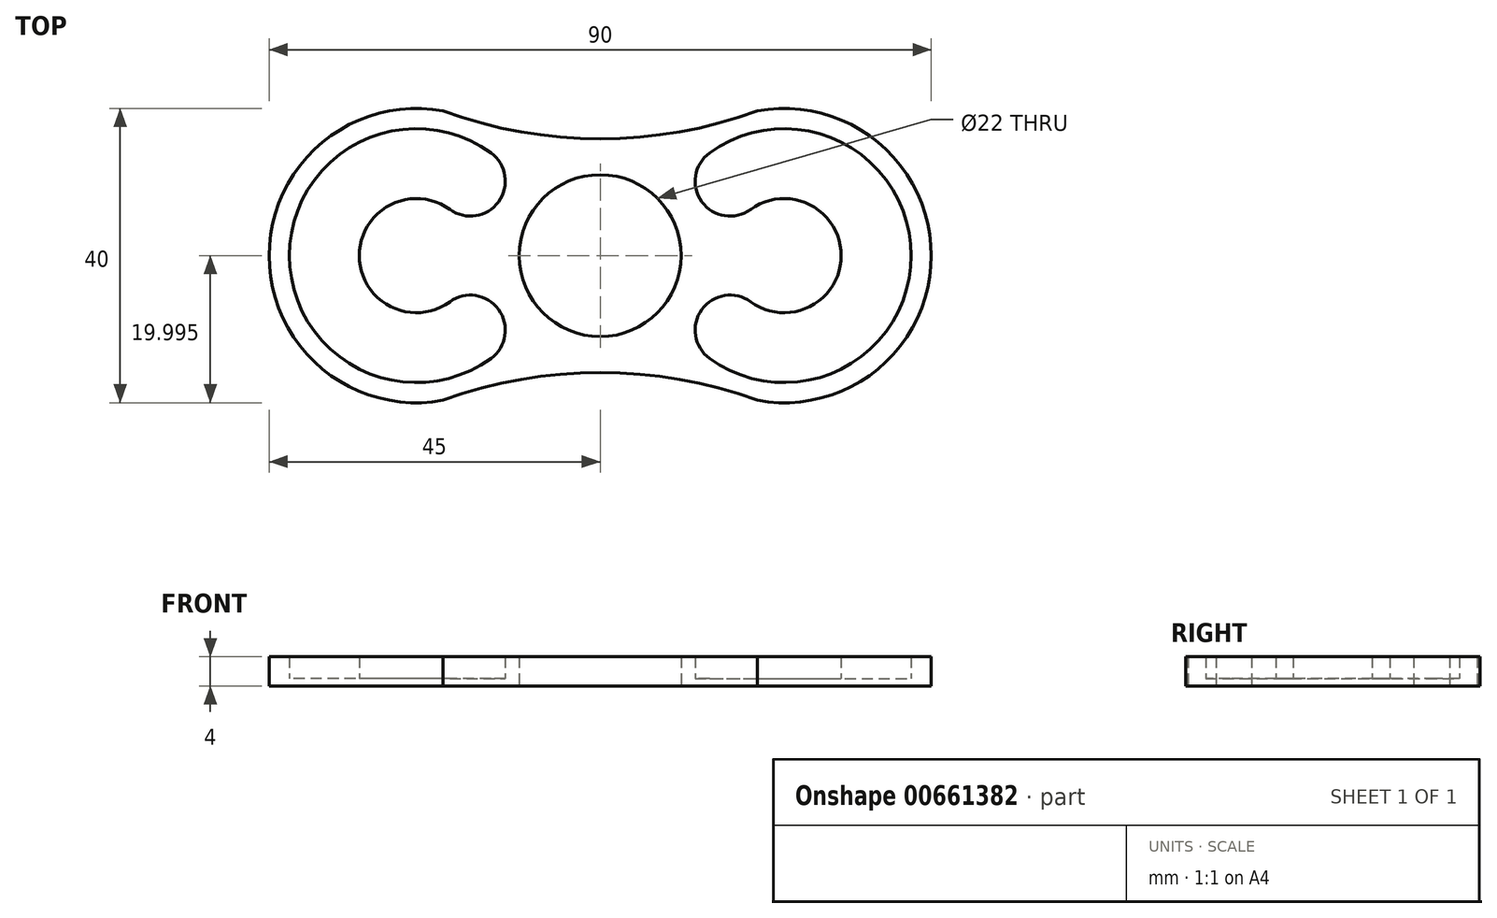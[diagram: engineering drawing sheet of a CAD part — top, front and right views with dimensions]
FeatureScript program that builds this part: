
annotation { "Feature Type Name" : "Feature", "Feature Type Description" : "" }
export const myFeature = defineFeature(function(context is Context, id is Id, definition is map)
    precondition{}
    {
        {
            var Q0;
            Q0=qCreatedBy(makeId("Top.planeOp"),FACE);
            var sketch = newSketch(context, id + "F0", { "sketchPlane" : qUnion([Q0])});
            skCircle(sketch, "E0", {"center": v(25, 38.36) * mm, "radius": 11 * mm});
            skCircle(sketch, "E1", {"center": v(25, 38.36) * mm, "radius": 15 * mm});
            skCircle(sketch, "E2", {"center": v(0, 38.36) * mm, "radius": 20 * mm});
            skArc(sketch, "E3", {"start": v(3.66, 58.02) * mm, "mid": v(25, 54.23) * mm, "end": v(46.34, 58.02) * mm});
            skPoint(sketch, "E4", {"position": v(3.66, 18.7) * mm});
            skPoint(sketch, "E5", {"position": v(46.34, 18.7) * mm});
            skArc(sketch, "E6", {"start": v(46.34, 18.7) * mm, "mid": v(25, 22.48) * mm, "end": v(3.66, 18.7) * mm});
            skCircle(sketch, "E7", {"center": v(0, 38.36) * mm, "radius": 17.25 * mm});
            skLineSegment(sketch, "E8.anchor1", {"start": v(0, 38.36) * mm, "end": v(0, 23.86) * mm, "construction": true});
            skPoint(sketch, "E9", {"position": v(50, 38.36) * mm});
            skCircle(sketch, "E10", {"center": v(50, 38.36) * mm, "radius": 20 * mm});
            skCircle(sketch, "E11", {"center": v(50, 38.36) * mm, "radius": 17.25 * mm});
            skCircle(sketch, "E12", {"center": v(0, 38.36) * mm, "radius": 7.75 * mm});
            skLineSegment(sketch, "E13", {"start": v(0, 38.36) * mm, "end": v(0, 46.1) * mm});
            skLineSegment(sketch, "E14", {"start": v(0, 46.1) * mm, "end": v(0, 50.86) * mm});
            skCircle(sketch, "E15.1.0", {"center": v(7.35, 48.47) * mm, "radius": 4.75 * mm});
            skCircle(sketch, "E15.4.0", {"center": v(7.35, 28.24) * mm, "radius": 4.75 * mm});
            skLineSegment(sketch, "E15.anchor1", {"start": v(0, 38.36) * mm, "end": v(0, 50.86) * mm, "construction": true});
            skLineSegment(sketch, "E15.anchor2", {"start": v(0, 38.36) * mm, "end": v(0, 25.86) * mm, "construction": true});
            skCircle(sketch, "E16", {"center": v(50, 38.36) * mm, "radius": 7.75 * mm});
            skLineSegment(sketch, "E17", {"start": v(50, 38.36) * mm, "end": v(50, 46.1) * mm});
            skLineSegment(sketch, "E18", {"start": v(50, 46.1) * mm, "end": v(50, 50.86) * mm});
            skCircle(sketch, "E19.1.0", {"center": v(42.65, 48.47) * mm, "radius": 4.75 * mm});
            skCircle(sketch, "E19.4.0", {"center": v(42.65, 28.24) * mm, "radius": 4.75 * mm});
            skLineSegment(sketch, "E19.anchor1", {"start": v(50, 38.36) * mm, "end": v(50, 50.86) * mm, "construction": true});
            skLineSegment(sketch, "E19.anchor2", {"start": v(50, 38.36) * mm, "end": v(50, 25.86) * mm, "construction": true});
            skSolve(sketch);
        }
        {
            var Q0;
            {var subQ1=sQuery(id+"F0.wireOp",EDGE,"E2");var subQ6=sQuery(id+"F0.wireOp",EDGE,"E1");var subQ7=makeQuery(id+"F0.imprint","INTERSECT",VERTEX,{"disambiguationData":[OD(0.0)],"derivedFrom":[subQ6,subQ1]});Q0=makeQuery(id+"F0.imprint","IMPRINT",FACE,{"disambiguationData":[TD([[makeQuery(id+"F0.imprint","IMPRINT",EDGE,{"disambiguationData":[TD([[subQ7,-1.0]])],"derivedFrom":subQ6}),-1.0]])]});}
            var Q1;
            {var subQ0=sQuery(id+"F0.wireOp",EDGE,"E12");var subQ1=makeQuery(id+"F0.imprint","IMPRINT",VERTEX,{"derivedFrom":subQ0});Q1=makeQuery(id+"F0.imprint","IMPRINT",FACE,{"disambiguationData":[TD([[makeQuery(id+"F0.imprint","IMPRINT",EDGE,{"disambiguationData":[TD([[subQ1,1.0]])],"derivedFrom":subQ0}),1.0]])]});}
            var Q2;
            {var subQ5=sQuery(id+"F0.wireOp",EDGE,"E7");var subQ6=sQuery(id+"F0.wireOp",EDGE,"E1");var subQ9=makeQuery(id+"F0.imprint","INTERSECT",VERTEX,{"disambiguationData":[OD(0.0)],"derivedFrom":[subQ6,subQ5]});Q2=makeQuery(id+"F0.imprint","IMPRINT",FACE,{"disambiguationData":[TD([[makeQuery(id+"F0.imprint","IMPRINT",EDGE,{"disambiguationData":[TD([[subQ9,-1.0]])],"derivedFrom":subQ6}),-1.0]])]});}
            var Q3;
            {var subQ0=sQuery(id+"F0.wireOp",EDGE,"E7");var subQ1=sQuery(id+"F0.wireOp",EDGE,"E0");var subQ2=makeQuery(id+"F0.imprint","INTERSECT",VERTEX,{"disambiguationData":[OD(0.0)],"derivedFrom":[subQ1,subQ0]});Q3=makeQuery(id+"F0.imprint","IMPRINT",FACE,{"disambiguationData":[TD([[makeQuery(id+"F0.imprint","IMPRINT",EDGE,{"disambiguationData":[TD([[subQ2,-1.0]])],"derivedFrom":subQ1}),-1.0]])]});}
            var Q4;
            {var subQ0=sQuery(id+"F0.wireOp",EDGE,"E2");var subQ1=sQuery(id+"F0.wireOp",EDGE,"E0");var subQ2=makeQuery(id+"F0.imprint","INTERSECT",VERTEX,{"disambiguationData":[OD(0.0)],"derivedFrom":[subQ1,subQ0]});Q4=makeQuery(id+"F0.imprint","IMPRINT",FACE,{"disambiguationData":[TD([[makeQuery(id+"F0.imprint","IMPRINT",EDGE,{"disambiguationData":[TD([[subQ2,-1.0]])],"derivedFrom":subQ1}),-1.0]])]});}
            var Q5;
            {var subQ0=sQuery(id+"F0.wireOp",EDGE,"E10");var subQ1=sQuery(id+"F0.wireOp",EDGE,"E0");var subQ2=makeQuery(id+"F0.imprint","INTERSECT",VERTEX,{"disambiguationData":[OD(0.0)],"derivedFrom":[subQ1,subQ0]});Q5=makeQuery(id+"F0.imprint","IMPRINT",FACE,{"disambiguationData":[TD([[makeQuery(id+"F0.imprint","IMPRINT",EDGE,{"disambiguationData":[TD([[subQ2,-1.0]])],"derivedFrom":subQ1}),-1.0]])]});}
            var Q6;
            {var subQ0=sQuery(id+"F0.wireOp",EDGE,"E10");var subQ1=sQuery(id+"F0.wireOp",EDGE,"E0");var subQ2=makeQuery(id+"F0.imprint","INTERSECT",VERTEX,{"disambiguationData":[OD(0.0)],"derivedFrom":[subQ1,subQ0]});Q6=makeQuery(id+"F0.imprint","IMPRINT",FACE,{"disambiguationData":[TD([[makeQuery(id+"F0.imprint","IMPRINT",EDGE,{"disambiguationData":[TD([[subQ2,1.0]])],"derivedFrom":subQ1}),-1.0]])]});}
            var Q7;
            {var subQ0=sQuery(id+"F0.wireOp",EDGE,"E11");var subQ1=sQuery(id+"F0.wireOp",EDGE,"E0");var subQ2=makeQuery(id+"F0.imprint","INTERSECT",VERTEX,{"disambiguationData":[OD(0.0)],"derivedFrom":[subQ1,subQ0]});Q7=makeQuery(id+"F0.imprint","IMPRINT",FACE,{"disambiguationData":[TD([[makeQuery(id+"F0.imprint","IMPRINT",EDGE,{"disambiguationData":[TD([[subQ2,1.0]])],"derivedFrom":subQ1}),-1.0]])]});}
            var Q8;
            {var subQ0=sQuery(id+"F0.wireOp",EDGE,"E10");var subQ1=sQuery(id+"F0.wireOp",EDGE,"E0");var subQ2=makeQuery(id+"F0.imprint","INTERSECT",VERTEX,{"disambiguationData":[OD(1.0)],"derivedFrom":[subQ1,subQ0]});Q8=makeQuery(id+"F0.imprint","IMPRINT",FACE,{"disambiguationData":[TD([[makeQuery(id+"F0.imprint","IMPRINT",EDGE,{"disambiguationData":[TD([[subQ2,-1.0]])],"derivedFrom":subQ1}),-1.0]])]});}
            var Q9;
            {var subQ0=sQuery(id+"F0.wireOp",EDGE,"E2");var subQ1=sQuery(id+"F0.wireOp",EDGE,"E0");var subQ2=makeQuery(id+"F0.imprint","INTERSECT",VERTEX,{"disambiguationData":[OD(1.0)],"derivedFrom":[subQ1,subQ0]});Q9=makeQuery(id+"F0.imprint","IMPRINT",FACE,{"disambiguationData":[TD([[makeQuery(id+"F0.imprint","IMPRINT",EDGE,{"disambiguationData":[TD([[subQ2,-1.0]])],"derivedFrom":subQ1}),-1.0]])]});}
            var Q10;
            {var subQ0=sQuery(id+"F0.wireOp",EDGE,"E2");var subQ1=sQuery(id+"F0.wireOp",EDGE,"E1");var subQ2=makeQuery(id+"F0.imprint","INTERSECT",VERTEX,{"disambiguationData":[OD(1.0)],"derivedFrom":[subQ1,subQ0]});Q10=makeQuery(id+"F0.imprint","IMPRINT",FACE,{"disambiguationData":[TD([[makeQuery(id+"F0.imprint","IMPRINT",EDGE,{"disambiguationData":[TD([[subQ2,-1.0]])],"derivedFrom":subQ1}),-1.0]])]});}
            var Q11;
            {var subQ0=sQuery(id+"F0.wireOp",EDGE,"E10");var subQ1=sQuery(id+"F0.wireOp",EDGE,"E1");var subQ2=makeQuery(id+"F0.imprint","INTERSECT",VERTEX,{"disambiguationData":[OD(0.0)],"derivedFrom":[subQ1,subQ0]});Q11=makeQuery(id+"F0.imprint","IMPRINT",FACE,{"disambiguationData":[TD([[makeQuery(id+"F0.imprint","IMPRINT",EDGE,{"disambiguationData":[TD([[subQ2,-1.0]])],"derivedFrom":subQ1}),-1.0]])]});}
            var Q12;
            {var subQ0=sQuery(id+"F0.wireOp",EDGE,"E7");var subQ1=sQuery(id+"F0.wireOp",EDGE,"E0");var subQ2=makeQuery(id+"F0.imprint","INTERSECT",VERTEX,{"disambiguationData":[OD(1.0)],"derivedFrom":[subQ1,subQ0]});Q12=makeQuery(id+"F0.imprint","IMPRINT",FACE,{"disambiguationData":[TD([[makeQuery(id+"F0.imprint","IMPRINT",EDGE,{"disambiguationData":[TD([[subQ2,-1.0]])],"derivedFrom":subQ1}),-1.0]])]});}
            var Q13;
            {var subQ0=sQuery(id+"F0.wireOp",EDGE,"E10");var subQ10=sQuery(id+"F0.wireOp",EDGE,"E1");var subQ11=makeQuery(id+"F0.imprint","INTERSECT",VERTEX,{"disambiguationData":[OD(0.0)],"derivedFrom":[subQ10,subQ0]});Q13=makeQuery(id+"F0.imprint","IMPRINT",FACE,{"disambiguationData":[TD([[makeQuery(id+"F0.imprint","IMPRINT",EDGE,{"disambiguationData":[TD([[subQ11,1.0]])],"derivedFrom":subQ10}),-1.0]])]});}
            var Q14;
            {var subQ5=sQuery(id+"F0.wireOp",EDGE,"E11");var subQ6=sQuery(id+"F0.wireOp",EDGE,"E1");var subQ9=makeQuery(id+"F0.imprint","INTERSECT",VERTEX,{"disambiguationData":[OD(0.0)],"derivedFrom":[subQ6,subQ5]});Q14=makeQuery(id+"F0.imprint","IMPRINT",FACE,{"disambiguationData":[TD([[makeQuery(id+"F0.imprint","IMPRINT",EDGE,{"disambiguationData":[TD([[subQ9,1.0]])],"derivedFrom":subQ6}),-1.0]])]});}
            var Q15;
            {var subQ0=sQuery(id+"F0.wireOp",EDGE,"E16");var subQ1=makeQuery(id+"F0.imprint","IMPRINT",VERTEX,{"derivedFrom":subQ0});Q15=makeQuery(id+"F0.imprint","IMPRINT",FACE,{"disambiguationData":[TD([[makeQuery(id+"F0.imprint","IMPRINT",EDGE,{"disambiguationData":[TD([[subQ1,-1.0]])],"derivedFrom":subQ0}),1.0]])]});}
            extrude(context, id + "F1", {"entities" : qUnion([Q0, Q1, Q2, Q3, Q4, Q5, Q6, Q7, Q8, Q9, Q10, Q11, Q12, Q13, Q14, Q15]), "depth" : 4 * mm, "offsetDistance" : 25 * mm});
        }
        {
            var Q0;
            {var subQ0=sQuery(id+"F0.wireOp",EDGE,"E15.1.0");var subQ1=makeQuery(id+"F0.imprint","INTERSECT",VERTEX,{"derivedFrom":[sQuery(id+"F0.wireOp",EDGE,"E7"),subQ0]});Q0=makeQuery(id+"F0.imprint","IMPRINT",FACE,{"disambiguationData":[TD([[makeQuery(id+"F0.imprint","IMPRINT",EDGE,{"disambiguationData":[TD([[subQ1,-1.0]])],"derivedFrom":subQ0}),1.0]])]});}
            var Q1;
            {var subQ3=sQuery(id+"F0.wireOp",EDGE,"E12");var subQ5=makeQuery(id+"F0.imprint","IMPRINT",VERTEX,{"derivedFrom":subQ3});Q1=makeQuery(id+"F0.imprint","IMPRINT",FACE,{"disambiguationData":[TD([[makeQuery(id+"F0.imprint","IMPRINT",EDGE,{"disambiguationData":[TD([[subQ5,1.0]])],"derivedFrom":subQ3}),-1.0]])]});}
            var Q2;
            {var subQ0=sQuery(id+"F0.wireOp",EDGE,"E15.4.0");var subQ1=makeQuery(id+"F0.imprint","INTERSECT",VERTEX,{"derivedFrom":[sQuery(id+"F0.wireOp",EDGE,"E7"),subQ0]});Q2=makeQuery(id+"F0.imprint","IMPRINT",FACE,{"disambiguationData":[TD([[makeQuery(id+"F0.imprint","IMPRINT",EDGE,{"disambiguationData":[TD([[subQ1,-1.0]])],"derivedFrom":subQ0}),1.0]])]});}
            var Q3;
            {var subQ0=sQuery(id+"F0.wireOp",EDGE,"E19.1.0");var subQ1=makeQuery(id+"F0.imprint","INTERSECT",VERTEX,{"derivedFrom":[sQuery(id+"F0.wireOp",EDGE,"E11"),subQ0]});Q3=makeQuery(id+"F0.imprint","IMPRINT",FACE,{"disambiguationData":[TD([[makeQuery(id+"F0.imprint","IMPRINT",EDGE,{"disambiguationData":[TD([[subQ1,-1.0]])],"derivedFrom":subQ0}),1.0]])]});}
            var Q4;
            {var subQ3=sQuery(id+"F0.wireOp",EDGE,"E16");var subQ5=makeQuery(id+"F0.imprint","IMPRINT",VERTEX,{"derivedFrom":subQ3});Q4=makeQuery(id+"F0.imprint","IMPRINT",FACE,{"disambiguationData":[TD([[makeQuery(id+"F0.imprint","IMPRINT",EDGE,{"disambiguationData":[TD([[subQ5,-1.0]])],"derivedFrom":subQ3}),-1.0]])]});}
            var Q5;
            {var subQ0=sQuery(id+"F0.wireOp",EDGE,"E19.4.0");var subQ1=makeQuery(id+"F0.imprint","INTERSECT",VERTEX,{"derivedFrom":[sQuery(id+"F0.wireOp",EDGE,"E11"),subQ0]});Q5=makeQuery(id+"F0.imprint","IMPRINT",FACE,{"disambiguationData":[TD([[makeQuery(id+"F0.imprint","IMPRINT",EDGE,{"disambiguationData":[TD([[subQ1,-1.0]])],"derivedFrom":subQ0}),1.0]])]});}
            extrude(context, id + "F2", {"entities" : qUnion([Q0, Q1, Q2, Q3, Q4, Q5]), "operationType" : NewBodyOperationType.ADD, "depth" : 1 * mm, "offsetDistance" : 25 * mm});
        }
    });
